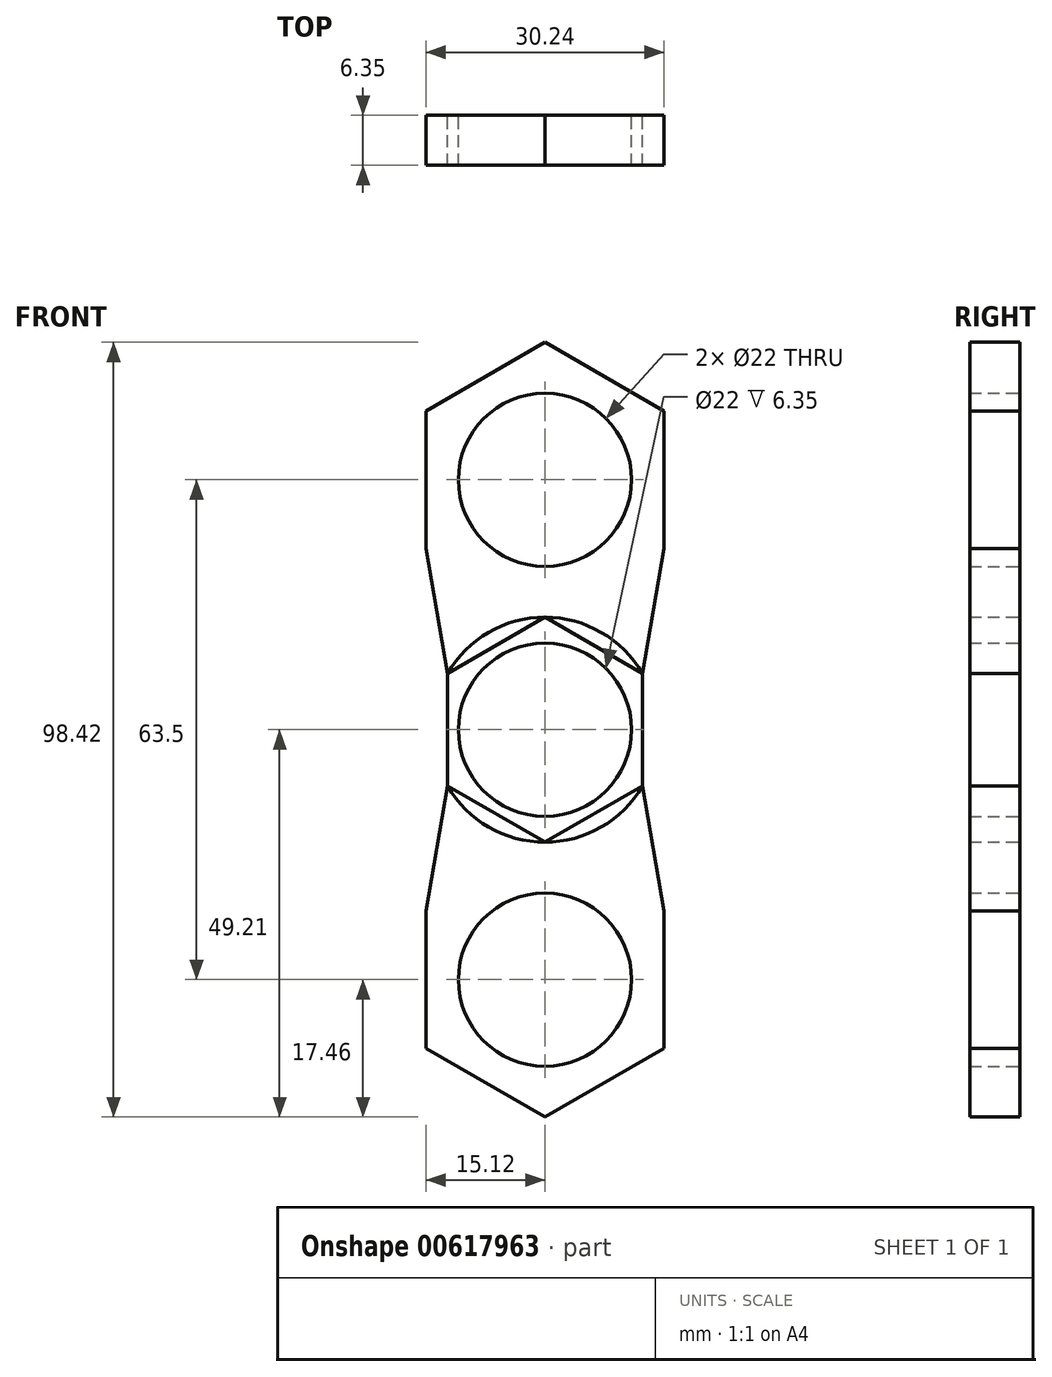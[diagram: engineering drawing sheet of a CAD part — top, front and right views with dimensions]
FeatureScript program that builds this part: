
annotation { "Feature Type Name" : "Feature", "Feature Type Description" : "" }
export const myFeature = defineFeature(function(context is Context, id is Id, definition is map)
    precondition{}
    {
        {
            var Q0;
            Q0=qCreatedBy(makeId("Front.planeOp"),FACE);
            var sketch = newSketch(context, id + "F0", { "sketchPlane" : qUnion([Q0])});
            skCircle(sketch, "E0", {"center": v(0, 0) * mm, "radius": 14.29 * mm});
            skCircle(sketch, "E1", {"center": v(0, 0) * mm, "radius": 11 * mm});
            skCircle(sketch, "E2", {"center": v(0, 31.75) * mm, "radius": 14.29 * mm});
            skCircle(sketch, "E3", {"center": v(0, 31.75) * mm, "radius": 11 * mm});
            skCircle(sketch, "E4", {"center": v(0, -31.75) * mm, "radius": 11 * mm});
            skCircle(sketch, "E5", {"center": v(0, -31.75) * mm, "radius": 14.29 * mm});
            skCircle(sketch, "E6.cCircle", {"center": v(0, 31.75) * mm, "radius": 17.46 * mm, "construction": true});
            skLineSegment(sketch, "E6.0", {"start": v(0, 14.29) * mm, "end": v(-15.12, 23.02) * mm});
            skLineSegment(sketch, "E6.1", {"start": v(-15.12, 23.02) * mm, "end": v(-15.12, 40.48) * mm});
            skLineSegment(sketch, "E6.2", {"start": v(-15.12, 40.48) * mm, "end": v(0, 49.21) * mm});
            skLineSegment(sketch, "E6.3", {"start": v(0, 49.21) * mm, "end": v(15.12, 40.48) * mm});
            skLineSegment(sketch, "E6.4", {"start": v(15.12, 40.48) * mm, "end": v(15.12, 23.02) * mm});
            skLineSegment(sketch, "E6.5", {"start": v(15.12, 23.02) * mm, "end": v(0, 14.29) * mm});
            skCircle(sketch, "E7.cCircle", {"center": v(0, 0) * mm, "radius": 14.29 * mm, "construction": true});
            skLineSegment(sketch, "E7.0", {"start": v(0, 14.29) * mm, "end": v(12.37, 7.14) * mm});
            skLineSegment(sketch, "E7.1", {"start": v(12.37, 7.14) * mm, "end": v(12.37, -7.14) * mm});
            skLineSegment(sketch, "E7.2", {"start": v(12.37, -7.14) * mm, "end": v(0, -14.29) * mm});
            skLineSegment(sketch, "E7.3", {"start": v(0, -14.29) * mm, "end": v(-12.37, -7.14) * mm});
            skLineSegment(sketch, "E7.4", {"start": v(-12.37, -7.14) * mm, "end": v(-12.37, 7.14) * mm});
            skLineSegment(sketch, "E7.5", {"start": v(-12.37, 7.14) * mm, "end": v(0, 14.29) * mm});
            skCircle(sketch, "E8.cCircle", {"center": v(0, -31.75) * mm, "radius": 17.46 * mm, "construction": true});
            skLineSegment(sketch, "E8.0", {"start": v(0, -14.29) * mm, "end": v(15.12, -23.02) * mm});
            skLineSegment(sketch, "E8.1", {"start": v(15.12, -23.02) * mm, "end": v(15.12, -40.48) * mm});
            skLineSegment(sketch, "E8.2", {"start": v(15.12, -40.48) * mm, "end": v(0, -49.21) * mm});
            skLineSegment(sketch, "E8.3", {"start": v(0, -49.21) * mm, "end": v(-15.12, -40.48) * mm});
            skLineSegment(sketch, "E8.4", {"start": v(-15.12, -40.48) * mm, "end": v(-15.12, -23.02) * mm});
            skLineSegment(sketch, "E8.5", {"start": v(-15.12, -23.02) * mm, "end": v(0, -14.29) * mm});
            skLineSegment(sketch, "E9", {"start": v(-15.12, 23.02) * mm, "end": v(-12.37, 7.14) * mm});
            skLineSegment(sketch, "E10", {"start": v(15.12, 23.02) * mm, "end": v(12.37, 7.14) * mm});
            skLineSegment(sketch, "E11", {"start": v(12.37, -7.14) * mm, "end": v(15.12, -23.02) * mm});
            skLineSegment(sketch, "E12", {"start": v(-12.37, -7.14) * mm, "end": v(-15.12, -23.02) * mm});
            skSolve(sketch);
        }
        {
            var Q0;
            {var subQ0=sQuery(id+"F0.wireOp",EDGE,"E8.5");Q0=makeQuery(id+"F0.imprint","IMPRINT",FACE,{"disambiguationData":[TD([[makeQuery(id+"F0.imprint","IMPRINT",EDGE,{"derivedFrom":subQ0}),1.0]])]});}
            var Q1;
            {var subQ3=sQuery(id+"F0.wireOp",EDGE,"E8.0");Q1=makeQuery(id+"F0.imprint","IMPRINT",FACE,{"disambiguationData":[TD([[makeQuery(id+"F0.imprint","IMPRINT",EDGE,{"derivedFrom":subQ3}),1.0]])]});}
            var Q2;
            Q2=makeQuery(id+"F0.imprint","IMPRINT",FACE,{"disambiguationData":[TD([[makeQuery(id+"F0.imprint","IMPRINT",EDGE,{"derivedFrom":sQuery(id+"F0.wireOp",EDGE,"E2")}),-1.0]])]});
            var Q3;
            Q3=makeQuery(id+"F0.imprint","IMPRINT",FACE,{"disambiguationData":[TD([[makeQuery(id+"F0.imprint","IMPRINT",EDGE,{"derivedFrom":sQuery(id+"F0.wireOp",EDGE,"E5")}),-1.0]])]});
            var Q4;
            Q4=makeQuery(id+"F0.imprint","IMPRINT",FACE,{"disambiguationData":[TD([[makeQuery(id+"F0.imprint","IMPRINT",EDGE,{"derivedFrom":sQuery(id+"F0.wireOp",EDGE,"E1")}),-1.0]])]});
            var Q5;
            Q5=makeQuery(id+"F0.imprint","IMPRINT",FACE,{"disambiguationData":[TD([[makeQuery(id+"F0.imprint","IMPRINT",EDGE,{"derivedFrom":sQuery(id+"F0.wireOp",EDGE,"E4")}),-1.0]])]});
            var Q6;
            Q6=makeQuery(id+"F0.imprint","IMPRINT",FACE,{"disambiguationData":[TD([[makeQuery(id+"F0.imprint","IMPRINT",EDGE,{"derivedFrom":sQuery(id+"F0.wireOp",EDGE,"E2")}),1.0]])]});
            var Q7;
            {var subQ1=sQuery(id+"F0.wireOp",EDGE,"E6.0");Q7=makeQuery(id+"F0.imprint","IMPRINT",FACE,{"disambiguationData":[TD([[makeQuery(id+"F0.imprint","IMPRINT",EDGE,{"derivedFrom":subQ1}),1.0]])]});}
            var Q8;
            {var subQ1=sQuery(id+"F0.wireOp",EDGE,"E6.5");Q8=makeQuery(id+"F0.imprint","IMPRINT",FACE,{"disambiguationData":[TD([[makeQuery(id+"F0.imprint","IMPRINT",EDGE,{"derivedFrom":subQ1}),1.0]])]});}
            extrude(context, id + "F1", {"entities" : qUnion([Q0, Q1, Q2, Q3, Q4, Q5, Q6, Q7, Q8]), "depth" : 6.35 * mm, "offsetDistance" : 25.4 * mm});
        }
    });
